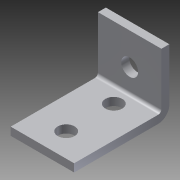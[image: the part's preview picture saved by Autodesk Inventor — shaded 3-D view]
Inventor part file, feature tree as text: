
AUTODESK INVENTOR PART (.ipt)
format: ipt  version: 2013 (Build 170138000, 138)  size: 167,936 bytes
history: native  units: in
note: dims shown in document units (in); Inventor stores cm internally (conversion verified against a paired STEP export)
features: sheet_metal_op x4, other x4, sketch x3
ambient origin geometry x8: Origin, YZ Plane, XZ Plane, XY Plane, X Axis, Y Axis, Z Axis, Center Point
bodies: Solid1 (feature_tree)
feature tree (11):
  sheet_metal_op  "Face1"
  sheet_metal_op  "Flange1"
  sketch  "Sketch1"  dims[d0=1.0in]
  other  "Plate1"
  sketch  "Sketch2"  dims[d1=1.5in]
  other  "Plate2"
  sheet_metal_op  "Bend1"
  sheet_metal_op  "Corner1"
  sketch  "Sketch3"  dims[d2=0.266in d3=0.266in d4=0.375in d5=0.375in d6=0.5in d7=0.5in d8=0.125in d9=0.125in d10=0.0625in d11=0.25in d12=0.125in d13=1.0in d14=90.0deg d15=0.05in d16=0.5in d17=0.125in d18=0.125in d19=0.266in d20=0.5in d21=0.5in d22=0.125in d23=0.0in]
  other  "Cut1"
  other  "Definition1"
